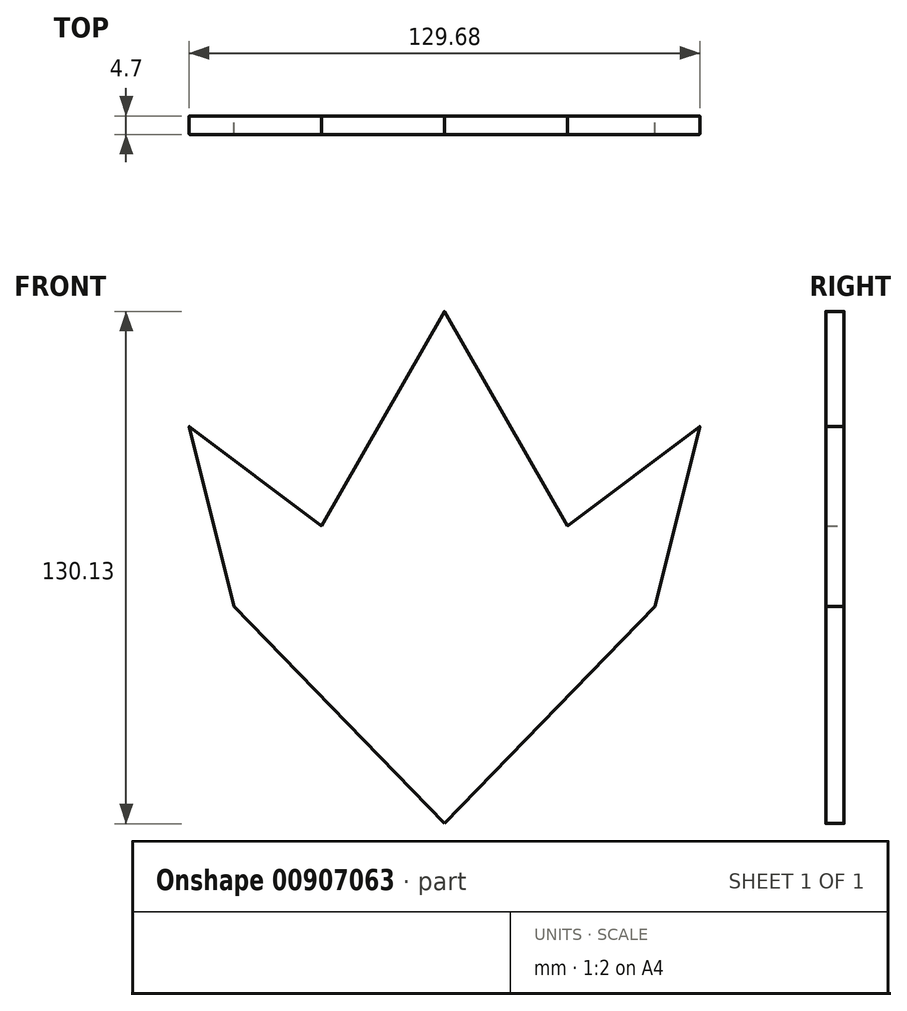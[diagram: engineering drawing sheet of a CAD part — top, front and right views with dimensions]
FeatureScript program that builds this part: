
annotation { "Feature Type Name" : "Feature", "Feature Type Description" : "" }
export const myFeature = defineFeature(function(context is Context, id is Id, definition is map)
    precondition{}
    {
        {
            var Q0;
            Q0=qCreatedBy(makeId("Front.planeOp"),FACE);
            var sketch = newSketch(context, id + "F0", { "sketchPlane" : qUnion([Q0])});
            skLineSegment(sketch, "E0", {"start": v(0, 75) * mm, "end": v(-8.16, 34.7) * mm});
            skLineSegment(sketch, "E1", {"start": v(-8.16, -8.53) * mm, "end": v(-36.87, 13.09) * mm});
            skLineSegment(sketch, "E2", {"start": v(-36.87, 13.09) * mm, "end": v(-31.26, 20.55) * mm});
            skLineSegment(sketch, "E3", {"start": v(-39.62, 20.55) * mm, "end": v(-53.42, 0) * mm});
            skLineSegment(sketch, "E4", {"start": v(-53.42, 0) * mm, "end": v(-39.62, 9.25) * mm});
            skLineSegment(sketch, "E5", {"start": v(-39.62, 9.25) * mm, "end": v(-4.46, -17.23) * mm});
            skPoint(sketch, "E6", {"position": v(0, -17.23) * mm});
            skLineSegment(sketch, "E7", {"start": v(-31.26, 20.55) * mm, "end": v(-64.84, 45.84) * mm});
            skLineSegment(sketch, "E8", {"start": v(-64.84, 45.84) * mm, "end": v(-39.62, 20.55) * mm});
            skLineSegment(sketch, "E9", {"start": v(-4.46, -17.23) * mm, "end": v(0, -38.85) * mm});
            skLineSegment(sketch, "E10.MirrorCS", {"start": v(0, 75) * mm, "end": v(8.16, 34.7) * mm});
            skLineSegment(sketch, "E11.MirrorCS", {"start": v(36.87, 13.09) * mm, "end": v(31.26, 20.55) * mm});
            skLineSegment(sketch, "E12.MirrorCS", {"start": v(39.62, 20.55) * mm, "end": v(53.42, 0) * mm});
            skLineSegment(sketch, "E13.MirrorCS", {"start": v(53.42, 0) * mm, "end": v(39.62, 9.25) * mm});
            skLineSegment(sketch, "E14.MirrorCS", {"start": v(31.26, 20.55) * mm, "end": v(64.84, 45.84) * mm});
            skLineSegment(sketch, "E15.MirrorCS", {"start": v(64.84, 45.84) * mm, "end": v(39.62, 20.55) * mm});
            skLineSegment(sketch, "E16.MirrorCS", {"start": v(8.16, -8.53) * mm, "end": v(36.87, 13.09) * mm});
            skLineSegment(sketch, "E17.MirrorCS", {"start": v(39.62, 9.25) * mm, "end": v(4.46, -17.23) * mm});
            skLineSegment(sketch, "E18.MirrorCS", {"start": v(4.46, -17.23) * mm, "end": v(0, -38.85) * mm});
            skLineSegment(sketch, "E19", {"start": v(53.42, 0) * mm, "end": v(0, -38.85) * mm});
            skLineSegment(sketch, "E20", {"start": v(0, -38.85) * mm, "end": v(-53.42, 0) * mm});
            skLineSegment(sketch, "E21", {"start": v(-53.42, 0) * mm, "end": v(-64.84, 45.84) * mm});
            skLineSegment(sketch, "E22", {"start": v(53.42, 0) * mm, "end": v(64.84, 45.84) * mm});
            skLineSegment(sketch, "E23", {"start": v(53.42, 0) * mm, "end": v(4.46, -17.23) * mm});
            skLineSegment(sketch, "E24", {"start": v(-53.42, 0) * mm, "end": v(-4.46, -17.23) * mm});
            skLineSegment(sketch, "E25", {"start": v(8.16, -8.53) * mm, "end": v(0, -17.23) * mm});
            skLineSegment(sketch, "E26", {"start": v(-8.16, -8.53) * mm, "end": v(0, -17.23) * mm});
            skLineSegment(sketch, "E27", {"start": v(8.16, 34.7) * mm, "end": v(31.26, 20.55) * mm});
            skLineSegment(sketch, "E28", {"start": v(8.16, -8.53) * mm, "end": v(31.26, 20.55) * mm});
            skLineSegment(sketch, "E29", {"start": v(-31.26, 20.55) * mm, "end": v(-8.16, 34.7) * mm});
            skLineSegment(sketch, "E30", {"start": v(-31.26, 20.55) * mm, "end": v(-8.16, -8.53) * mm});
            skLineSegment(sketch, "E31", {"start": v(-8.16, 34.7) * mm, "end": v(-8.16, -8.53) * mm});
            skLineSegment(sketch, "E32", {"start": v(8.16, 34.7) * mm, "end": v(8.16, -8.53) * mm});
            skLineSegment(sketch, "E33", {"start": v(0, 75) * mm, "end": v(31.26, 20.55) * mm});
            skLineSegment(sketch, "E34", {"start": v(0, 75) * mm, "end": v(-31.26, 20.55) * mm});
            skLineSegment(sketch, "E35", {"start": v(0, 75) * mm, "end": v(0, 0) * mm});
            skLineSegment(sketch, "E36", {"start": v(0, 0) * mm, "end": v(0, -17.23) * mm});
            skLineSegment(sketch, "E37", {"start": v(-8.16, 34.7) * mm, "end": v(8.16, -8.53) * mm});
            skLineSegment(sketch, "E38", {"start": v(8.16, 34.7) * mm, "end": v(-8.16, -8.53) * mm});
            skLineSegment(sketch, "E39", {"start": v(0, 0) * mm, "end": v(-8.16, -8.53) * mm});
            skLineSegment(sketch, "E40", {"start": v(0, 0) * mm, "end": v(8.16, -8.53) * mm});
            skLineSegment(sketch, "E41", {"start": v(-8.16, -8.53) * mm, "end": v(-4.46, -17.23) * mm});
            skLineSegment(sketch, "E42", {"start": v(8.16, -8.53) * mm, "end": v(4.46, -17.23) * mm});
            skLineSegment(sketch, "E43", {"start": v(4.46, -17.23) * mm, "end": v(0, -23.89) * mm});
            skLineSegment(sketch, "E44", {"start": v(0, -23.89) * mm, "end": v(-4.46, -17.23) * mm});
            skLineSegment(sketch, "E45", {"start": v(0, -23.89) * mm, "end": v(0, -38.85) * mm});
            skLineSegment(sketch, "E46", {"start": v(53.42, 0) * mm, "end": v(12.46, -23.89) * mm});
            skLineSegment(sketch, "E47", {"start": v(12.46, -23.89) * mm, "end": v(4.46, -17.23) * mm});
            skLineSegment(sketch, "E48", {"start": v(12.46, -23.89) * mm, "end": v(0, -38.85) * mm});
            skLineSegment(sketch, "E49", {"start": v(-53.42, 0) * mm, "end": v(-12.02, -23.89) * mm});
            skLineSegment(sketch, "E50", {"start": v(-12.02, -23.89) * mm, "end": v(-4.46, -17.23) * mm});
            skLineSegment(sketch, "E51", {"start": v(-12.02, -23.89) * mm, "end": v(0, -38.85) * mm});
            skLineSegment(sketch, "E52", {"start": v(-53.42, 0) * mm, "end": v(-39.62, 0) * mm});
            skLineSegment(sketch, "E53", {"start": v(-39.62, 0) * mm, "end": v(-4.46, -17.23) * mm});
            skLineSegment(sketch, "E54", {"start": v(-39.62, 0) * mm, "end": v(-39.62, 9.25) * mm});
            skLineSegment(sketch, "E55", {"start": v(53.42, 0) * mm, "end": v(39.62, 0) * mm});
            skLineSegment(sketch, "E56", {"start": v(39.62, 0) * mm, "end": v(39.62, 9.25) * mm});
            skLineSegment(sketch, "E57", {"start": v(39.62, 0) * mm, "end": v(4.46, -17.23) * mm});
            skLineSegment(sketch, "E58", {"start": v(-64.84, 45.84) * mm, "end": v(-50.1, 20.55) * mm});
            skLineSegment(sketch, "E59", {"start": v(-50.1, 20.55) * mm, "end": v(-53.42, 0) * mm});
            skLineSegment(sketch, "E60", {"start": v(-50.1, 20.55) * mm, "end": v(-39.62, 20.55) * mm});
            skLineSegment(sketch, "E61", {"start": v(64.84, 45.84) * mm, "end": v(51.22, 20.55) * mm});
            skLineSegment(sketch, "E62", {"start": v(51.22, 20.55) * mm, "end": v(53.42, 0) * mm});
            skLineSegment(sketch, "E63", {"start": v(51.22, 20.55) * mm, "end": v(39.62, 20.55) * mm});
            skLineSegment(sketch, "E64", {"start": v(-8.16, -8.53) * mm, "end": v(-17.2, 15.42) * mm});
            skLineSegment(sketch, "E65", {"start": v(-17.2, 15.42) * mm, "end": v(-8.16, 34.7) * mm});
            skLineSegment(sketch, "E66", {"start": v(-17.2, 15.42) * mm, "end": v(-31.26, 20.55) * mm});
            skLineSegment(sketch, "E67", {"start": v(8.16, -8.53) * mm, "end": v(16.54, 15.42) * mm});
            skLineSegment(sketch, "E68", {"start": v(16.54, 15.42) * mm, "end": v(8.16, 34.7) * mm});
            skLineSegment(sketch, "E69", {"start": v(16.54, 15.42) * mm, "end": v(31.26, 20.55) * mm});
            skLineSegment(sketch, "E70", {"start": v(-8.16, 34.7) * mm, "end": v(-14.41, 38.9) * mm});
            skLineSegment(sketch, "E71", {"start": v(-14.41, 38.9) * mm, "end": v(0, 75) * mm});
            skLineSegment(sketch, "E72", {"start": v(-14.41, 38.9) * mm, "end": v(-31.26, 20.55) * mm});
            skLineSegment(sketch, "E73", {"start": v(8.16, 34.7) * mm, "end": v(13.45, 38.9) * mm});
            skLineSegment(sketch, "E74", {"start": v(13.45, 38.9) * mm, "end": v(31.26, 20.55) * mm});
            skLineSegment(sketch, "E75", {"start": v(13.45, 38.9) * mm, "end": v(0, 75) * mm});
            skLineSegment(sketch, "E76", {"start": v(8.16, 34.7) * mm, "end": v(0, 51.37) * mm});
            skLineSegment(sketch, "E77", {"start": v(-8.16, 34.7) * mm, "end": v(0, 51.37) * mm});
            skLineSegment(sketch, "E78", {"start": v(-53.42, 0) * mm, "end": v(0, -55.13) * mm});
            skLineSegment(sketch, "E79", {"start": v(0, -55.13) * mm, "end": v(53.42, 0) * mm});
            skLineSegment(sketch, "E80", {"start": v(0, -46.74) * mm, "end": v(53.42, 0) * mm});
            skLineSegment(sketch, "E81", {"start": v(0, -46.74) * mm, "end": v(-53.42, 0) * mm});
            skLineSegment(sketch, "E82", {"start": v(9.02, -38.85) * mm, "end": v(0, -55.13) * mm});
            skLineSegment(sketch, "E83", {"start": v(-9.02, -38.85) * mm, "end": v(0, -55.13) * mm});
            skLineSegment(sketch, "E84", {"start": v(-9.02, -32.3) * mm, "end": v(0, -46.74) * mm});
            skLineSegment(sketch, "E85", {"start": v(9.02, -32.3) * mm, "end": v(0, -46.74) * mm});
            skLineSegment(sketch, "E86", {"start": v(-9.02, -32.3) * mm, "end": v(-12.02, -23.89) * mm});
            skLineSegment(sketch, "E87", {"start": v(9.02, -32.3) * mm, "end": v(12.46, -23.89) * mm});
            skLineSegment(sketch, "E88", {"start": v(9.02, -38.85) * mm, "end": v(9.02, -32.3) * mm});
            skLineSegment(sketch, "E89", {"start": v(-9.02, -38.85) * mm, "end": v(-9.02, -32.3) * mm});
            skLineSegment(sketch, "E90", {"start": v(-4.46, -17.23) * mm, "end": v(-6.8, -23.89) * mm});
            skLineSegment(sketch, "E91", {"start": v(-6.8, -23.89) * mm, "end": v(0, -38.85) * mm});
            skLineSegment(sketch, "E92", {"start": v(-6.8, -23.89) * mm, "end": v(-12.02, -23.89) * mm});
            skLineSegment(sketch, "E93", {"start": v(4.46, -17.23) * mm, "end": v(6.8, -23.89) * mm});
            skLineSegment(sketch, "E94", {"start": v(6.8, -23.89) * mm, "end": v(12.46, -23.89) * mm});
            skLineSegment(sketch, "E95", {"start": v(6.8, -23.89) * mm, "end": v(0, -38.85) * mm});
            skLineSegment(sketch, "E96", {"start": v(0, -38.85) * mm, "end": v(0, -41.83) * mm});
            skLineSegment(sketch, "E97", {"start": v(0, -41.83) * mm, "end": v(9.02, -32.3) * mm});
            skLineSegment(sketch, "E98", {"start": v(0, -41.83) * mm, "end": v(-9.02, -32.3) * mm});
            skLineSegment(sketch, "E99", {"start": v(0, -41.83) * mm, "end": v(0, -46.74) * mm});
            skLineSegment(sketch, "E100", {"start": v(0, -46.74) * mm, "end": v(0, -50.22) * mm});
            skLineSegment(sketch, "E101", {"start": v(9.02, -38.85) * mm, "end": v(0, -50.22) * mm});
            skLineSegment(sketch, "E102", {"start": v(0, -50.22) * mm, "end": v(-9.02, -38.85) * mm});
            skLineSegment(sketch, "E103", {"start": v(0, -50.22) * mm, "end": v(0, -55.13) * mm});
            skLineSegment(sketch, "E104", {"start": v(-9.02, -32.3) * mm, "end": v(-7.91, -37.65) * mm});
            skLineSegment(sketch, "E105", {"start": v(-7.91, -37.65) * mm, "end": v(0, -46.74) * mm});
            skLineSegment(sketch, "E106", {"start": v(9.02, -32.3) * mm, "end": v(7.91, -37.65) * mm});
            skLineSegment(sketch, "E107", {"start": v(7.91, -37.65) * mm, "end": v(0, -46.74) * mm});
            skSolve(sketch);
        }
        {
            var Q0;
            Q0=makeQuery(id+"F0.imprint","IMPRINT",FACE,{"disambiguationData":[TD([[makeQuery(id+"F0.imprint","IMPRINT",EDGE,{"derivedFrom":sQuery(id+"F0.wireOp",EDGE,"E8")}),-1.0]])]});
            var Q1;
            Q1=makeQuery(id+"F0.imprint","IMPRINT",FACE,{"disambiguationData":[TD([[makeQuery(id+"F0.imprint","IMPRINT",EDGE,{"derivedFrom":sQuery(id+"F0.wireOp",EDGE,"E4")}),-1.0]])]});
            var Q2;
            Q2=makeQuery(id+"F0.imprint","IMPRINT",FACE,{"disambiguationData":[TD([[makeQuery(id+"F0.imprint","IMPRINT",EDGE,{"derivedFrom":sQuery(id+"F0.wireOp",EDGE,"E5")}),-1.0]])]});
            var Q3;
            Q3=makeQuery(id+"F0.imprint","IMPRINT",FACE,{"disambiguationData":[TD([[makeQuery(id+"F0.imprint","IMPRINT",EDGE,{"derivedFrom":sQuery(id+"F0.wireOp",EDGE,"E1")}),-1.0]])]});
            var Q4;
            Q4=makeQuery(id+"F0.imprint","IMPRINT",FACE,{"disambiguationData":[TD([[makeQuery(id+"F0.imprint","IMPRINT",EDGE,{"derivedFrom":sQuery(id+"F0.wireOp",EDGE,"E11.MirrorCS")}),1.0]])]});
            var Q5;
            Q5=makeQuery(id+"F0.imprint","IMPRINT",FACE,{"disambiguationData":[TD([[makeQuery(id+"F0.imprint","IMPRINT",EDGE,{"derivedFrom":sQuery(id+"F0.wireOp",EDGE,"E21")}),-1.0]])]});
            var Q6;
            Q6=makeQuery(id+"F0.imprint","IMPRINT",FACE,{"disambiguationData":[TD([[makeQuery(id+"F0.imprint","IMPRINT",EDGE,{"derivedFrom":sQuery(id+"F0.wireOp",EDGE,"E22")}),1.0]])]});
            var Q7;
            Q7=makeQuery(id+"F0.imprint","IMPRINT",FACE,{"disambiguationData":[TD([[makeQuery(id+"F0.imprint","IMPRINT",EDGE,{"derivedFrom":sQuery(id+"F0.wireOp",EDGE,"E3")}),-1.0]])]});
            var Q8;
            {var subQ0=sQuery(id+"F0.wireOp",EDGE,"E96");Q8=makeQuery(id+"F0.imprint","IMPRINT",FACE,{"disambiguationData":[TD([[makeQuery(id+"F0.imprint","IMPRINT",EDGE,{"derivedFrom":subQ0}),-1.0]])]});}
            var Q9;
            Q9=makeQuery(id+"F0.imprint","IMPRINT",FACE,{"disambiguationData":[TD([[makeQuery(id+"F0.imprint","IMPRINT",EDGE,{"derivedFrom":sQuery(id+"F0.wireOp",EDGE,"E31")}),-1.0]])]});
            var Q10;
            {var subQ0=sQuery(id+"F0.wireOp",EDGE,"E96");Q10=makeQuery(id+"F0.imprint","IMPRINT",FACE,{"disambiguationData":[TD([[makeQuery(id+"F0.imprint","IMPRINT",EDGE,{"derivedFrom":subQ0}),1.0]])]});}
            var Q11;
            Q11=makeQuery(id+"F0.imprint","IMPRINT",FACE,{"disambiguationData":[TD([[makeQuery(id+"F0.imprint","IMPRINT",EDGE,{"derivedFrom":sQuery(id+"F0.wireOp",EDGE,"E30")}),1.0]])]});
            var Q12;
            {var subQ0=sQuery(id+"F0.wireOp",EDGE,"E51");Q12=makeQuery(id+"F0.imprint","IMPRINT",FACE,{"disambiguationData":[TD([[makeQuery(id+"F0.imprint","IMPRINT",EDGE,{"derivedFrom":subQ0}),-1.0]])]});}
            var Q13;
            {var subQ0=sQuery(id+"F0.wireOp",EDGE,"E31");Q13=makeQuery(id+"F0.imprint","IMPRINT",FACE,{"disambiguationData":[TD([[makeQuery(id+"F0.imprint","IMPRINT",EDGE,{"derivedFrom":subQ0}),1.0]])]});}
            var Q14;
            Q14=makeQuery(id+"F0.imprint","IMPRINT",FACE,{"disambiguationData":[TD([[makeQuery(id+"F0.imprint","IMPRINT",EDGE,{"derivedFrom":sQuery(id+"F0.wireOp",EDGE,"E9")}),1.0]])]});
            var Q15;
            {var subQ0=sQuery(id+"F0.wireOp",EDGE,"E49");Q15=makeQuery(id+"F0.imprint","IMPRINT",FACE,{"disambiguationData":[TD([[makeQuery(id+"F0.imprint","IMPRINT",EDGE,{"derivedFrom":subQ0}),-1.0]])]});}
            var Q16;
            {var subQ0=sQuery(id+"F0.wireOp",EDGE,"E32");Q16=makeQuery(id+"F0.imprint","IMPRINT",FACE,{"disambiguationData":[TD([[makeQuery(id+"F0.imprint","IMPRINT",EDGE,{"derivedFrom":subQ0}),-1.0]])]});}
            var Q17;
            Q17=makeQuery(id+"F0.imprint","IMPRINT",FACE,{"disambiguationData":[TD([[makeQuery(id+"F0.imprint","IMPRINT",EDGE,{"derivedFrom":sQuery(id+"F0.wireOp",EDGE,"E9")}),-1.0]])]});
            var Q18;
            {var subQ3=sQuery(id+"F0.wireOp",EDGE,"E89");Q18=makeQuery(id+"F0.imprint","IMPRINT",FACE,{"disambiguationData":[TD([[makeQuery(id+"F0.imprint","IMPRINT",EDGE,{"derivedFrom":subQ3}),1.0]])]});}
            var Q19;
            Q19=makeQuery(id+"F0.imprint","IMPRINT",FACE,{"disambiguationData":[TD([[makeQuery(id+"F0.imprint","IMPRINT",EDGE,{"derivedFrom":sQuery(id+"F0.wireOp",EDGE,"E32")}),1.0]])]});
            var Q20;
            {var subQ0=sQuery(id+"F0.wireOp",EDGE,"E77");Q20=makeQuery(id+"F0.imprint","IMPRINT",FACE,{"disambiguationData":[TD([[makeQuery(id+"F0.imprint","IMPRINT",EDGE,{"derivedFrom":subQ0}),-1.0]])]});}
            var Q21;
            Q21=makeQuery(id+"F0.imprint","IMPRINT",FACE,{"disambiguationData":[TD([[makeQuery(id+"F0.imprint","IMPRINT",EDGE,{"derivedFrom":sQuery(id+"F0.wireOp",EDGE,"E1")}),1.0]])]});
            var Q22;
            Q22=makeQuery(id+"F0.imprint","IMPRINT",FACE,{"disambiguationData":[TD([[makeQuery(id+"F0.imprint","IMPRINT",EDGE,{"derivedFrom":sQuery(id+"F0.wireOp",EDGE,"E23")}),-1.0]])]});
            var Q23;
            {var subQ0=sQuery(id+"F0.wireOp",EDGE,"E76");Q23=makeQuery(id+"F0.imprint","IMPRINT",FACE,{"disambiguationData":[TD([[makeQuery(id+"F0.imprint","IMPRINT",EDGE,{"derivedFrom":subQ0}),1.0]])]});}
            var Q24;
            Q24=makeQuery(id+"F0.imprint","IMPRINT",FACE,{"disambiguationData":[TD([[makeQuery(id+"F0.imprint","IMPRINT",EDGE,{"derivedFrom":sQuery(id+"F0.wireOp",EDGE,"E11.MirrorCS")}),-1.0]])]});
            var Q25;
            Q25=makeQuery(id+"F0.imprint","IMPRINT",FACE,{"disambiguationData":[TD([[makeQuery(id+"F0.imprint","IMPRINT",EDGE,{"derivedFrom":sQuery(id+"F0.wireOp",EDGE,"E12.MirrorCS")}),1.0]])]});
            var Q26;
            {var subQ0=sQuery(id+"F0.wireOp",EDGE,"E40");Q26=makeQuery(id+"F0.imprint","IMPRINT",FACE,{"disambiguationData":[TD([[makeQuery(id+"F0.imprint","IMPRINT",EDGE,{"derivedFrom":subQ0}),1.0]])]});}
            var Q27;
            Q27=makeQuery(id+"F0.imprint","IMPRINT",FACE,{"disambiguationData":[TD([[makeQuery(id+"F0.imprint","IMPRINT",EDGE,{"derivedFrom":sQuery(id+"F0.wireOp",EDGE,"E25")}),1.0]])]});
            var Q28;
            Q28=makeQuery(id+"F0.imprint","IMPRINT",FACE,{"disambiguationData":[TD([[makeQuery(id+"F0.imprint","IMPRINT",EDGE,{"derivedFrom":sQuery(id+"F0.wireOp",EDGE,"E13.MirrorCS")}),1.0]])]});
            var Q29;
            Q29=makeQuery(id+"F0.imprint","IMPRINT",FACE,{"disambiguationData":[TD([[makeQuery(id+"F0.imprint","IMPRINT",EDGE,{"derivedFrom":sQuery(id+"F0.wireOp",EDGE,"E24")}),1.0]])]});
            var Q30;
            {var subQ0=sQuery(id+"F0.wireOp",EDGE,"E39");Q30=makeQuery(id+"F0.imprint","IMPRINT",FACE,{"disambiguationData":[TD([[makeQuery(id+"F0.imprint","IMPRINT",EDGE,{"derivedFrom":subQ0}),-1.0]])]});}
            var Q31;
            Q31=makeQuery(id+"F0.imprint","IMPRINT",FACE,{"disambiguationData":[TD([[makeQuery(id+"F0.imprint","IMPRINT",EDGE,{"derivedFrom":sQuery(id+"F0.wireOp",EDGE,"E15.MirrorCS")}),1.0]])]});
            var Q32;
            Q32=makeQuery(id+"F0.imprint","IMPRINT",FACE,{"disambiguationData":[TD([[makeQuery(id+"F0.imprint","IMPRINT",EDGE,{"derivedFrom":sQuery(id+"F0.wireOp",EDGE,"E25")}),-1.0]])]});
            var Q33;
            Q33=makeQuery(id+"F0.imprint","IMPRINT",FACE,{"disambiguationData":[TD([[makeQuery(id+"F0.imprint","IMPRINT",EDGE,{"derivedFrom":sQuery(id+"F0.wireOp",EDGE,"E47")}),1.0]])]});
            var Q34;
            Q34=makeQuery(id+"F0.imprint","IMPRINT",FACE,{"disambiguationData":[TD([[makeQuery(id+"F0.imprint","IMPRINT",EDGE,{"derivedFrom":sQuery(id+"F0.wireOp",EDGE,"E17.MirrorCS")}),1.0]])]});
            var Q35;
            Q35=makeQuery(id+"F0.imprint","IMPRINT",FACE,{"disambiguationData":[TD([[makeQuery(id+"F0.imprint","IMPRINT",EDGE,{"derivedFrom":sQuery(id+"F0.wireOp",EDGE,"E26")}),1.0]])]});
            var Q36;
            Q36=makeQuery(id+"F0.imprint","IMPRINT",FACE,{"disambiguationData":[TD([[makeQuery(id+"F0.imprint","IMPRINT",EDGE,{"derivedFrom":sQuery(id+"F0.wireOp",EDGE,"E48")}),-1.0]])]});
            var Q37;
            Q37=makeQuery(id+"F0.imprint","IMPRINT",FACE,{"disambiguationData":[TD([[makeQuery(id+"F0.imprint","IMPRINT",EDGE,{"derivedFrom":sQuery(id+"F0.wireOp",EDGE,"E18.MirrorCS")}),-1.0]])]});
            var Q38;
            Q38=makeQuery(id+"F0.imprint","IMPRINT",FACE,{"disambiguationData":[TD([[makeQuery(id+"F0.imprint","IMPRINT",EDGE,{"derivedFrom":sQuery(id+"F0.wireOp",EDGE,"E27")}),-1.0]])]});
            var Q39;
            Q39=makeQuery(id+"F0.imprint","IMPRINT",FACE,{"disambiguationData":[TD([[makeQuery(id+"F0.imprint","IMPRINT",EDGE,{"derivedFrom":sQuery(id+"F0.wireOp",EDGE,"E50")}),-1.0]])]});
            var Q40;
            Q40=makeQuery(id+"F0.imprint","IMPRINT",FACE,{"disambiguationData":[TD([[makeQuery(id+"F0.imprint","IMPRINT",EDGE,{"derivedFrom":sQuery(id+"F0.wireOp",EDGE,"E18.MirrorCS")}),1.0]])]});
            var Q41;
            Q41=makeQuery(id+"F0.imprint","IMPRINT",FACE,{"disambiguationData":[TD([[makeQuery(id+"F0.imprint","IMPRINT",EDGE,{"derivedFrom":sQuery(id+"F0.wireOp",EDGE,"E27")}),1.0]])]});
            var Q42;
            Q42=makeQuery(id+"F0.imprint","IMPRINT",FACE,{"disambiguationData":[TD([[makeQuery(id+"F0.imprint","IMPRINT",EDGE,{"derivedFrom":sQuery(id+"F0.wireOp",EDGE,"E51")}),1.0]])]});
            var Q43;
            {var subQ0=sQuery(id+"F0.wireOp",EDGE,"E46");Q43=makeQuery(id+"F0.imprint","IMPRINT",FACE,{"disambiguationData":[TD([[makeQuery(id+"F0.imprint","IMPRINT",EDGE,{"derivedFrom":subQ0}),1.0]])]});}
            var Q44;
            Q44=makeQuery(id+"F0.imprint","IMPRINT",FACE,{"disambiguationData":[TD([[makeQuery(id+"F0.imprint","IMPRINT",EDGE,{"derivedFrom":sQuery(id+"F0.wireOp",EDGE,"E28")}),1.0]])]});
            var Q45;
            {var subQ3=sQuery(id+"F0.wireOp",EDGE,"E88");Q45=makeQuery(id+"F0.imprint","IMPRINT",FACE,{"disambiguationData":[TD([[makeQuery(id+"F0.imprint","IMPRINT",EDGE,{"derivedFrom":subQ3}),-1.0]])]});}
            var Q46;
            Q46=makeQuery(id+"F0.imprint","IMPRINT",FACE,{"disambiguationData":[TD([[makeQuery(id+"F0.imprint","IMPRINT",EDGE,{"derivedFrom":sQuery(id+"F0.wireOp",EDGE,"E29")}),-1.0]])]});
            var Q47;
            {var subQ0=sQuery(id+"F0.wireOp",EDGE,"E48");Q47=makeQuery(id+"F0.imprint","IMPRINT",FACE,{"disambiguationData":[TD([[makeQuery(id+"F0.imprint","IMPRINT",EDGE,{"derivedFrom":subQ0}),1.0]])]});}
            var Q48;
            Q48=makeQuery(id+"F0.imprint","IMPRINT",FACE,{"disambiguationData":[TD([[makeQuery(id+"F0.imprint","IMPRINT",EDGE,{"derivedFrom":sQuery(id+"F0.wireOp",EDGE,"E29")}),1.0]])]});
            var Q49;
            {var subQ0=sQuery(id+"F0.wireOp",EDGE,"E0");Q49=makeQuery(id+"F0.imprint","IMPRINT",FACE,{"disambiguationData":[TD([[makeQuery(id+"F0.imprint","IMPRINT",EDGE,{"derivedFrom":subQ0}),1.0]])]});}
            var Q50;
            Q50=makeQuery(id+"F0.imprint","IMPRINT",FACE,{"disambiguationData":[TD([[makeQuery(id+"F0.imprint","IMPRINT",EDGE,{"derivedFrom":sQuery(id+"F0.wireOp",EDGE,"E0")}),-1.0]])]});
            var Q51;
            {var subQ0=sQuery(id+"F0.wireOp",EDGE,"E10.MirrorCS");Q51=makeQuery(id+"F0.imprint","IMPRINT",FACE,{"disambiguationData":[TD([[makeQuery(id+"F0.imprint","IMPRINT",EDGE,{"derivedFrom":subQ0}),-1.0]])]});}
            var Q52;
            Q52=makeQuery(id+"F0.imprint","IMPRINT",FACE,{"disambiguationData":[TD([[makeQuery(id+"F0.imprint","IMPRINT",EDGE,{"derivedFrom":sQuery(id+"F0.wireOp",EDGE,"E10.MirrorCS")}),1.0]])]});
            var Q53;
            {var subQ0=sQuery(id+"F0.wireOp",EDGE,"E78");Q53=makeQuery(id+"F0.imprint","IMPRINT",FACE,{"disambiguationData":[TD([[makeQuery(id+"F0.imprint","IMPRINT",EDGE,{"derivedFrom":subQ0}),1.0]])]});}
            var Q54;
            Q54=makeQuery(id+"F0.imprint","IMPRINT",FACE,{"disambiguationData":[TD([[makeQuery(id+"F0.imprint","IMPRINT",EDGE,{"derivedFrom":sQuery(id+"F0.wireOp",EDGE,"E84")}),-1.0]])]});
            var Q55;
            Q55=makeQuery(id+"F0.imprint","IMPRINT",FACE,{"disambiguationData":[TD([[makeQuery(id+"F0.imprint","IMPRINT",EDGE,{"derivedFrom":sQuery(id+"F0.wireOp",EDGE,"E85")}),1.0]])]});
            var Q56;
            Q56=makeQuery(id+"F0.imprint","IMPRINT",FACE,{"disambiguationData":[TD([[makeQuery(id+"F0.imprint","IMPRINT",EDGE,{"derivedFrom":sQuery(id+"F0.wireOp",EDGE,"E83")}),1.0]])]});
            var Q57;
            {var subQ0=sQuery(id+"F0.wireOp",EDGE,"E100");Q57=makeQuery(id+"F0.imprint","IMPRINT",FACE,{"disambiguationData":[TD([[makeQuery(id+"F0.imprint","IMPRINT",EDGE,{"derivedFrom":subQ0}),-1.0]])]});}
            var Q58;
            Q58=makeQuery(id+"F0.imprint","IMPRINT",FACE,{"disambiguationData":[TD([[makeQuery(id+"F0.imprint","IMPRINT",EDGE,{"derivedFrom":sQuery(id+"F0.wireOp",EDGE,"E82")}),-1.0]])]});
            var Q59;
            Q59=makeQuery(id+"F0.imprint","IMPRINT",FACE,{"disambiguationData":[TD([[makeQuery(id+"F0.imprint","IMPRINT",EDGE,{"derivedFrom":sQuery(id+"F0.wireOp",EDGE,"E84")}),1.0]])]});
            var Q60;
            Q60=makeQuery(id+"F0.imprint","IMPRINT",FACE,{"disambiguationData":[TD([[makeQuery(id+"F0.imprint","IMPRINT",EDGE,{"derivedFrom":sQuery(id+"F0.wireOp",EDGE,"E85")}),-1.0]])]});
            var Q61;
            {var subQ2=sQuery(id+"F0.wireOp",EDGE,"E88");Q61=makeQuery(id+"F0.imprint","IMPRINT",FACE,{"disambiguationData":[TD([[makeQuery(id+"F0.imprint","IMPRINT",EDGE,{"derivedFrom":subQ2}),1.0]])]});}
            var Q62;
            {var subQ0=sQuery(id+"F0.wireOp",EDGE,"E100");Q62=makeQuery(id+"F0.imprint","IMPRINT",FACE,{"disambiguationData":[TD([[makeQuery(id+"F0.imprint","IMPRINT",EDGE,{"derivedFrom":subQ0}),1.0]])]});}
            var Q63;
            {var subQ2=sQuery(id+"F0.wireOp",EDGE,"E89");Q63=makeQuery(id+"F0.imprint","IMPRINT",FACE,{"disambiguationData":[TD([[makeQuery(id+"F0.imprint","IMPRINT",EDGE,{"derivedFrom":subQ2}),-1.0]])]});}
            var Q64;
            {var subQ0=sQuery(id+"F0.wireOp",EDGE,"E79");Q64=makeQuery(id+"F0.imprint","IMPRINT",FACE,{"disambiguationData":[TD([[makeQuery(id+"F0.imprint","IMPRINT",EDGE,{"derivedFrom":subQ0}),1.0]])]});}
            var Q65;
            Q65=makeQuery(id+"F0.imprint","IMPRINT",FACE,{"disambiguationData":[TD([[makeQuery(id+"F0.imprint","IMPRINT",EDGE,{"derivedFrom":sQuery(id+"F0.wireOp",EDGE,"E34")}),1.0]])]});
            var Q66;
            Q66=makeQuery(id+"F0.imprint","IMPRINT",FACE,{"disambiguationData":[TD([[makeQuery(id+"F0.imprint","IMPRINT",EDGE,{"derivedFrom":sQuery(id+"F0.wireOp",EDGE,"E33")}),-1.0]])]});
            var Q67;
            Q67=makeQuery(id+"F0.imprint","IMPRINT",FACE,{"disambiguationData":[TD([[makeQuery(id+"F0.imprint","IMPRINT",EDGE,{"derivedFrom":sQuery(id+"F0.wireOp",EDGE,"E24")}),-1.0]])]});
            var Q68;
            Q68=makeQuery(id+"F0.imprint","IMPRINT",FACE,{"disambiguationData":[TD([[makeQuery(id+"F0.imprint","IMPRINT",EDGE,{"derivedFrom":sQuery(id+"F0.wireOp",EDGE,"E23")}),1.0]])]});
            extrude(context, id + "F1", {"entities" : qUnion([Q0, Q1, Q2, Q3, Q4, Q5, Q6, Q7, Q8, Q9, Q10, Q11, Q12, Q13, Q14, Q15, Q16, Q17, Q18, Q19, Q20, Q21, Q22, Q23, Q24, Q25, Q26, Q27, Q28, Q29, Q30, Q31, Q32, Q33, Q34, Q35, Q36, Q37, Q38, Q39, Q40, Q41, Q42, Q43, Q44, Q45, Q46, Q47, Q48, Q49, Q50, Q51, Q52, Q53, Q54, Q55, Q56, Q57, Q58, Q59, Q60, Q61, Q62, Q63, Q64, Q65, Q66, Q67, Q68]), "depth" : 4.7 * mm, "offsetDistance" : 25 * mm});
        }
        {
            var Q0;
            Q0=makeQuery(id+"F1.opExtrude","CAP_FACE",FACE,{"disambiguationData":[OSD([sQuery(id+"F0.wireOp",EDGE,"E7"),sQuery(id+"F0.wireOp",EDGE,"E14.MirrorCS"),sQuery(id+"F0.wireOp",EDGE,"E21"),sQuery(id+"F0.wireOp",EDGE,"E22"),sQuery(id+"F0.wireOp",EDGE,"E33"),sQuery(id+"F0.wireOp",EDGE,"E34"),sQuery(id+"F0.wireOp",EDGE,"E78"),sQuery(id+"F0.wireOp",EDGE,"E79")])],"isStart":false});
            var Q1;
            Q1=makeQuery(id+"F1.opExtrude","CAP_FACE",FACE,{"disambiguationData":[OSD([sQuery(id+"F0.wireOp",EDGE,"E7"),sQuery(id+"F0.wireOp",EDGE,"E14.MirrorCS"),sQuery(id+"F0.wireOp",EDGE,"E21"),sQuery(id+"F0.wireOp",EDGE,"E22"),sQuery(id+"F0.wireOp",EDGE,"E33"),sQuery(id+"F0.wireOp",EDGE,"E34"),sQuery(id+"F0.wireOp",EDGE,"E78"),sQuery(id+"F0.wireOp",EDGE,"E79")])],"isStart":true});
            fillet(context, id + "F2", {"entities" : qUnion([Q0, Q1]), "radius" : 0.02 * mm, "tangentPropagation" : true, "allowEdgeOverflow" : false});
        }
    });
